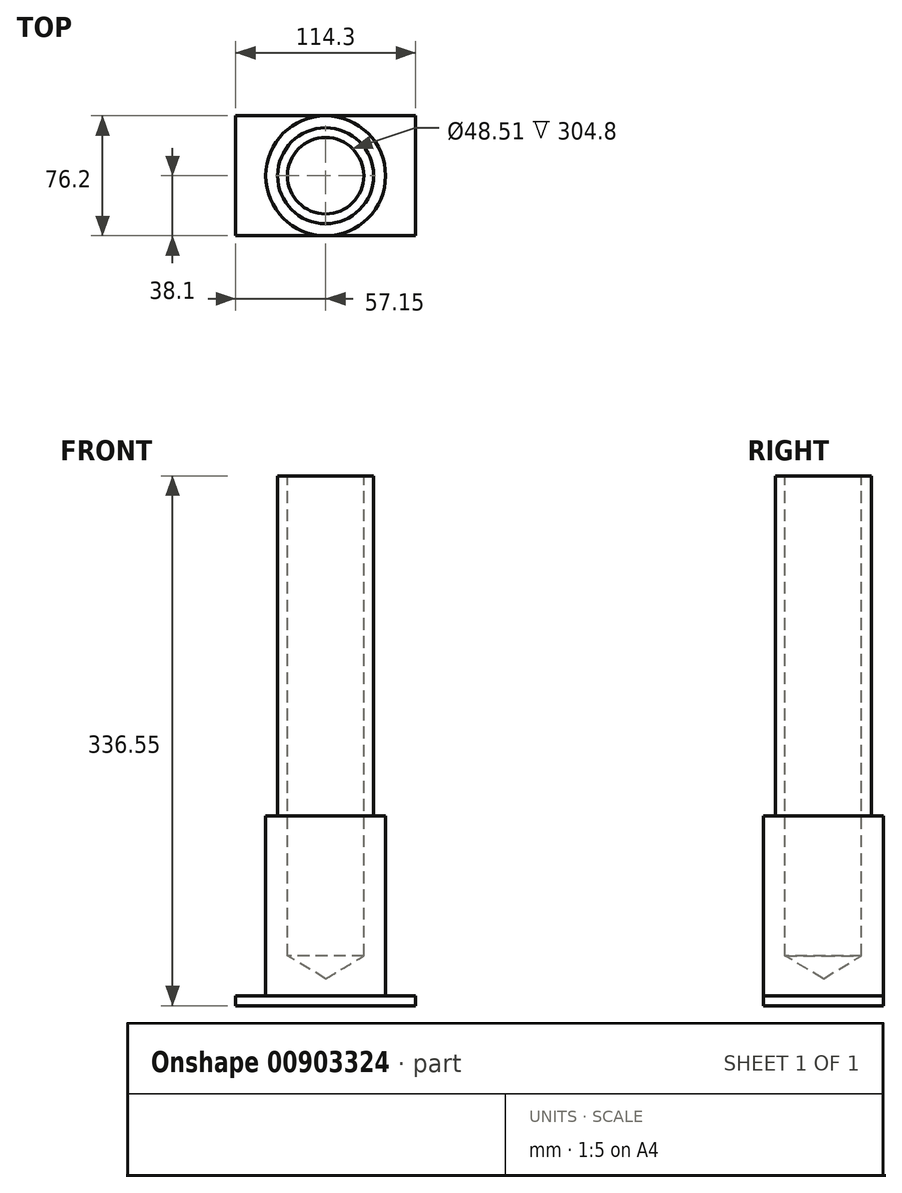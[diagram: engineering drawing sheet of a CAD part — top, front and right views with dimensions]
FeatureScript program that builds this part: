
annotation { "Feature Type Name" : "Feature", "Feature Type Description" : "" }
export const myFeature = defineFeature(function(context is Context, id is Id, definition is map)
    precondition{}
    {
        {
            var Q0;
            Q0=qCreatedBy(makeId("Top.planeOp"),FACE);
            var sketch = newSketch(context, id + "F0", { "sketchPlane" : qUnion([Q0])});
            skCircle(sketch, "E0", {"center": v(0, 0) * mm, "radius": 38.1 * mm});
            skSolve(sketch);
        }
        {
            var Q0;
            Q0=makeQuery(id+"F0.imprint","IMPRINT",FACE,{"disambiguationData":[TD([[makeQuery(id+"F0.imprint","IMPRINT",EDGE,{"derivedFrom":sQuery(id+"F0.wireOp",EDGE,"E0")}),1.0]])]});
            extrude(context, id + "F1", {"entities" : qUnion([Q0]), "depth" : 114.3 * mm, "offsetDistance" : 25.4 * mm});
        }
        {
            var Q0;
            Q0=makeQuery(id+"F1.opExtrude","CAP_FACE",FACE,{"disambiguationData":[OSD([sQuery(id+"F0.wireOp",EDGE,"E0")])],"isStart":false});
            var sketch = newSketch(context, id + "F2", { "sketchPlane" : qUnion([Q0])});
            skCircle(sketch, "E1", {"center": v(0, 0) * mm, "radius": 30.48 * mm});
            skSolve(sketch);
        }
        {
            var Q0;
            Q0=makeQuery(id+"F2.imprint","IMPRINT",FACE,{"disambiguationData":[TD([[makeQuery(id+"F2.imprint","IMPRINT",EDGE,{"derivedFrom":sQuery(id+"F2.wireOp",EDGE,"E1")}),1.0]])]});
            extrude(context, id + "F3", {"entities" : qUnion([Q0]), "operationType" : NewBodyOperationType.ADD, "depth" : 215.9 * mm, "offsetDistance" : 25.4 * mm});
        }
        {
            var Q0;
            Q0=makeQuery(id+"F3.opExtrude","CAP_FACE",FACE,{"disambiguationData":[OSD([sQuery(id+"F2.wireOp",EDGE,"E1")])],"isStart":false});
            var sketch = newSketch(context, id + "F4", { "sketchPlane" : qUnion([Q0])});
            skCircle(sketch, "E2", {"center": v(0, 0) * mm, "radius": 24.26 * mm});
            skSolve(sketch);
        }
        {
            var Q0;
            Q0=sQuery(id+"F4.wireOp",VERTEX,"E2.center");
            var Q1;
            Q1=makeQuery(id+"F1.opExtrude","SWEPT_BODY",BODY,{"disambiguationData":[OSD([sQuery(id+"F0.wireOp",EDGE,"E0")])]});
            hole(context, id + "F5", {"style" : HoleStyle.SIMPLE, "endStyle" : HoleEndStyle.BLIND, "holeDiameter" : 48.5 * mm, "majorDiameter" : 6.35 * mm, "holeDepth" : 304.8 * mm, "isTappedThrough" : true, "tappedDepth" : 12.7 * mm, "tapClearance" : 3, "locations" : qUnion([Q0]), "scope" : qUnion([Q1])});
        }
        {
            var Q0;
            Q0=qCreatedBy(makeId("Top.planeOp"),FACE);
            var sketch = newSketch(context, id + "F6", { "sketchPlane" : qUnion([Q0])});
            skLineSegment(sketch, "E3.bottom", {"start": v(-57.15, 38.1) * mm, "end": v(57.15, 38.1) * mm});
            skLineSegment(sketch, "E3.top", {"start": v(-57.15, -38.1) * mm, "end": v(57.15, -38.1) * mm});
            skLineSegment(sketch, "E3.left", {"start": v(-57.15, 38.1) * mm, "end": v(-57.15, -38.1) * mm});
            skLineSegment(sketch, "E3.right", {"start": v(57.15, 38.1) * mm, "end": v(57.15, -38.1) * mm});
            skSolve(sketch);
        }
        {
            var Q0;
            Q0=makeQuery(id+"F6.imprint","IMPRINT",FACE,{"disambiguationData":[TD([[makeQuery(id+"F6.imprint","IMPRINT",EDGE,{"derivedFrom":sQuery(id+"F6.wireOp",EDGE,"E3.bottom")}),-1.0]])]});
            extrude(context, id + "F7", {"entities" : qUnion([Q0]), "operationType" : NewBodyOperationType.ADD, "oppositeDirection" : true, "depth" : 6.35 * mm, "offsetDistance" : 25.4 * mm});
        }
    });
